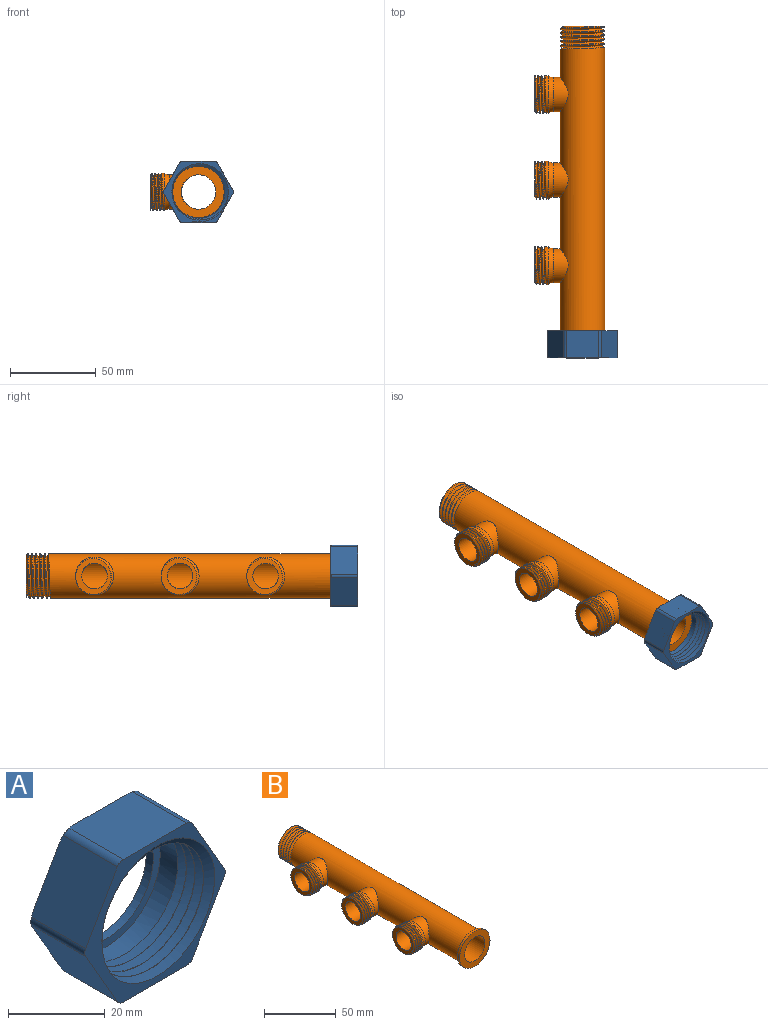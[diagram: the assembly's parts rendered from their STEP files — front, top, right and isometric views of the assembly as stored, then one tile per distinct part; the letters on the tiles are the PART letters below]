
ASSEMBLY  parts=2 mates=1
PART A: 29 faces, bbox 43.9x19.3x42.2 mm
  f0: cylinder r=15.45mm len=30.9mm, axis (0,1,0), area 510.3mm2, adj f3,f10,f26,f27,f28
  f1: cylinder r=15.45mm len=19.43mm, axis (0,1,0), area 2.6mm2, adj f2,f4,f27,f28
  f2: cylinder r=15.45mm len=30.9mm, axis (0,1,0), area 9.7mm2, adj f1,f3,f27,f28
  f3: cylinder r=15.45mm len=30.9mm, axis (0,1,0), area 9.7mm2, adj f0,f2,f27,f28
  f4: plane 42.7x37.75mm, normal (0,-1,0), area 270mm2, adj f1,f14,f15,f16,f17,f18,f19,f20
  f5: torus R=19.45mm, axis (0,1,0), area 3.3mm2, adj f12,f14,f15,f20
  f6: torus R=19.45mm, axis (0,1,0), area 3.3mm2, adj f12,f15,f16,f21
  f7: torus R=19.45mm, axis (0,1,0), area 3.3mm2, adj f12,f16,f17,f22
  f8: torus R=19.45mm, axis (0,1,0), area 3.3mm2, adj f12,f17,f18,f23
  f9: torus R=19.45mm, axis (0,1,0), area 3.3mm2, adj f12,f14,f19,f25
  f10: plane 30.9x30.9mm, normal (0,-1,0), area 179.6mm2, adj f0,f13
  f11: torus R=19.45mm, axis (0,1,0), area 3.3mm2, adj f12,f18,f19,f24
  f12: plane 38.9x36mm, normal (0,1,0), area 532mm2, adj f5,f6,f7,f8,f9,f11,f13,f14
  f13: cylinder r=13.47mm len=26.95mm, axis (0,1,0), area 175.1mm2, adj f10,f12
  f14: plane 16.07x16.07mm, normal (-0.87,0,-0.5), area 295.4mm2, adj f4,f5,f9,f12,f20,f25
  f15: plane 16.07x16.07mm, normal (-0.87,0,0.5), area 295.4mm2, adj f4,f5,f6,f12,f20,f21
  f16: plane 18.54x16.07mm, normal (0,0,1), area 295.4mm2, adj f4,f6,f7,f12,f21,f22
  f17: plane 16.07x16.07mm, normal (0.87,0,0.5), area 295.4mm2, adj f4,f7,f8,f12,f22,f23
  f18: plane 16.07x16.07mm, normal (0.87,0,-0.5), area 295.4mm2, adj f4,f8,f11,f12,f23,f24
  f19: plane 18.54x16.07mm, normal (0,0,-1), area 295.4mm2, adj f4,f9,f11,f12,f24,f25
  f20: cylinder r=2mm len=15.84mm, axis (0,-1,0), area 33.2mm2, adj f4,f5,f14,f15
  f21: cylinder r=2mm len=15.84mm, axis (0,-1,0), area 33.2mm2, adj f4,f6,f15,f16
  f22: cylinder r=2mm len=15.84mm, axis (0,-1,0), area 33.2mm2, adj f4,f7,f16,f17
  f23: cylinder r=2mm len=15.84mm, axis (0,-1,0), area 33.2mm2, adj f4,f8,f17,f18
  f24: cylinder r=2mm len=15.84mm, axis (0,-1,0), area 33.2mm2, adj f4,f11,f18,f19
  f25: cylinder r=2mm len=15.84mm, axis (0,-1,0), area 33.2mm2, adj f4,f9,f14,f19
  f26: plane 2.4x2.08mm, normal (0,0,-1), area 2.5mm2, adj f0,f27,f28
  f27: bspline ~40.48x35.06mm, area 934.5mm2, adj f0,f1,f2,f3,f4,f26,f28
  f28: bspline ~40.48x35.06mm, area 817.6mm2, adj f0,f1,f2,f3,f4,f26,f27
PART B: 39 faces, bbox 45.2x184.3x31.2 mm
  f0: cylinder r=10mm len=182mm, axis (0,1,0), area 10856.4mm2, adj f8,f16,f24,f32,f34
  f1: cylinder r=13mm len=167.5mm, axis (0,1,0), area 12543.2mm2, adj f7,f15,f23,f31,f35,f37,f38
  f2: cylinder r=13mm len=12.4mm, axis (0,1,0), area 4.1mm2, adj f3,f8,f36
  f3: cylinder r=13mm len=26mm, axis (0,1,0), area 40.9mm2, adj f2,f4,f36,f37
  f4: cylinder r=13mm len=26mm, axis (0,1,0), area 40.8mm2, adj f3,f5,f36,f37
  f5: cylinder r=13mm len=26mm, axis (0,1,0), area 40.9mm2, adj f4,f6,f36,f37
  f6: cylinder r=13mm len=26mm, axis (0,1,0), area 40.8mm2, adj f5,f7,f36,f37
  f7: cylinder r=13mm len=26mm, axis (0,1,0), area 40.7mm2, adj f1,f6,f36,f37
  f8: plane 25.89x25.86mm, normal (0,1,0), area 162.7mm2, adj f0,f2,f36,f37
  f9: bspline ~25.58x22.15mm, area 370.2mm2, adj f10,f11,f13,f14
  f10: bspline ~25.58x22.15mm, area 419.4mm2, adj f9,f11,f13,f14
  f11: plane 1.7x1.47mm, normal (0,0,-1), area 1.3mm2, adj f9,f10,f14
  f12: torus R=15mm, axis (-1,0,0), area 217.5mm2, adj f14,f15
  f13: plane 21.98x21.95mm, normal (-1,0,0), area 167.1mm2, adj f9,f10,f14,f16
  f14: cylinder r=11.07mm len=22.15mm, axis (1,0,0), area 138.7mm2, adj f9,f10,f11,f12,f13
  f15: cylinder r=10mm len=20mm, axis (1,0,0), area 384.5mm2, adj f1,f12
  f16: cylinder r=7.5mm len=21.39mm, axis (-1,0,0), area 1007.8mm2, adj f0,f13
  f17: bspline ~25.58x22.15mm, area 370.2mm2, adj f18,f19,f21,f22
  f18: bspline ~25.58x22.15mm, area 419.4mm2, adj f17,f19,f21,f22
  f19: plane 1.7x1.47mm, normal (0,0,-1), area 1.3mm2, adj f17,f18,f22
  f20: torus R=15mm, axis (-1,0,0), area 217.5mm2, adj f22,f23
  f21: plane 21.98x21.95mm, normal (-1,0,0), area 167.1mm2, adj f17,f18,f22,f24
  f22: cylinder r=11.07mm len=22.15mm, axis (1,0,0), area 138.7mm2, adj f17,f18,f19,f20,f21
  f23: cylinder r=10mm len=20mm, axis (1,0,0), area 384.5mm2, adj f1,f20
  f24: cylinder r=7.5mm len=21.39mm, axis (1,0,0), area 1007.8mm2, adj f0,f21
  f25: bspline ~25.58x22.15mm, area 370.2mm2, adj f26,f27,f29,f30
  f26: bspline ~25.58x22.15mm, area 419.4mm2, adj f25,f27,f29,f30
  f27: plane 1.7x1.47mm, normal (0,0,-1), area 1.3mm2, adj f25,f26,f30
  f28: torus R=15mm, axis (-1,0,0), area 217.5mm2, adj f30,f31
  f29: plane 21.98x21.95mm, normal (-1,0,0), area 167.1mm2, adj f25,f26,f30,f32
  f30: cylinder r=11.07mm len=22.15mm, axis (1,0,0), area 138.7mm2, adj f25,f26,f27,f28,f29
  f31: cylinder r=10mm len=20mm, axis (1,0,0), area 384.5mm2, adj f1,f28
  f32: cylinder r=7.5mm len=21.39mm, axis (1,0,0), area 1007.8mm2, adj f0,f29
  f33: cylinder r=15mm len=30mm, axis (0,1,0), area 188.5mm2, adj f34,f35
  f34: plane 30x30mm, normal (0,-1,0), area 392.7mm2, adj f0,f33
  f35: plane 30x30mm, normal (0,1,0), area 175.9mm2, adj f1,f33
  f36: bspline ~30.02x26mm, area 822.9mm2, adj f2,f3,f4,f5,f6,f7,f8,f37
  f37: bspline ~30.02x26mm, area 885.4mm2, adj f1,f3,f4,f5,f6,f7,f8,f36
  f38: plane 2x1.73mm, normal (0,0,-1), area 1.7mm2, adj f1,f36,f37
PLACE A t=(-61.73,44.48,-64.88)mm
PLACE B t=(-61.73,45.39,-64.88)mm
MATE revolute A.f0 <-> B.f0  axis (0,-1,0) through (-61.73,-134.61,-64.88)mm
